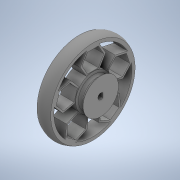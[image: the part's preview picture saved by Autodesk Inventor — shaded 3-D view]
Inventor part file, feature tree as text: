
AUTODESK INVENTOR PART (.ipt)
format: ipt  version: 2020 (Build 240168000, 168)  size: 424,448 bytes
history: native  units: in
note: dims shown in document units (in); Inventor stores cm internally (conversion verified against a paired STEP export)
features: sketch x4, extrude x2, revolve x2, projected_geometry x1
ambient origin geometry x8: Origin, YZ Plane, XZ Plane, XY Plane, X Axis, Y Axis, Z Axis, Center Point
bodies: Solid1 (feature_tree)
feature tree (9):
  extrude  "Extrusion1"  Depth=0.0394in
  sketch  "Sketch3"  dims[d6=0.7087in d7=0.1575in]
  revolve  "Revolution1"  [1 undecoded]
  extrude  "Extrusion2"  Depth=0.1575in
  revolve  "Revolution2"  [1 undecoded]
  sketch  "Sketch1"  dims[d0=0.1181in d1=0.0394in]
  sketch  "Sketch2"  dims[d3=1.6929in d4=0.1181in]
  projected_geometry  "Projected Loop1"
  sketch  "Sketch4"  dims[d8=0.0in d9=1.6929in d10=0.063in d11=0.0315in d16=0.2756in d17=0.0in d19=360.0deg d20=0.0787in d24=0.0394in d25=90.0deg d26=45.0deg d28=0.0079in d29=1.9685in d31=360.0deg]
note: 2 required parameter values undecoded (feature->parameter linkage not recoverable at this tier; creation-order binding heuristic only, values carry confidence <= 0.55)
